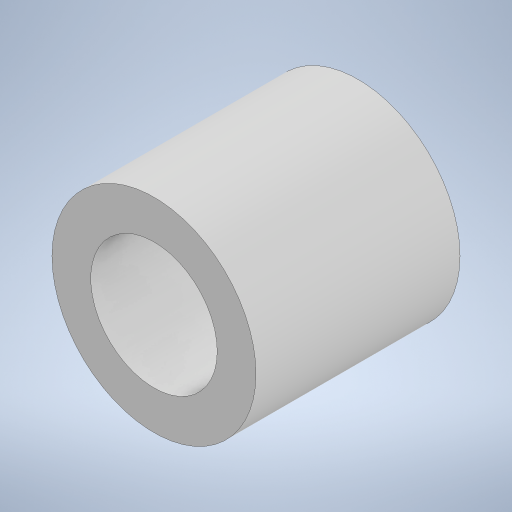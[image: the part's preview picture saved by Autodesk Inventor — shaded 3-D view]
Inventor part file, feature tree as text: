
AUTODESK INVENTOR PART (.ipt)
format: ipt  version: 2023 (Build 270158000, 158)  size: 206,336 bytes
history: native  units: in
note: dims shown in document units (in); Inventor stores cm internally (conversion verified against a paired STEP export)
features: extrude x1, sketch x1
ambient origin geometry x8: Origin, YZ Plane, XZ Plane, XY Plane, X Axis, Y Axis, Z Axis, Center Point
bodies: Solid1 (feature_tree)
feature tree (2):
  extrude  "Extrusion1"  Depth=0.3937in
  sketch  "Sketch1"  dims[d0=0.2441in d1=0.3937in d2=0.3937in d3=0.0in]
